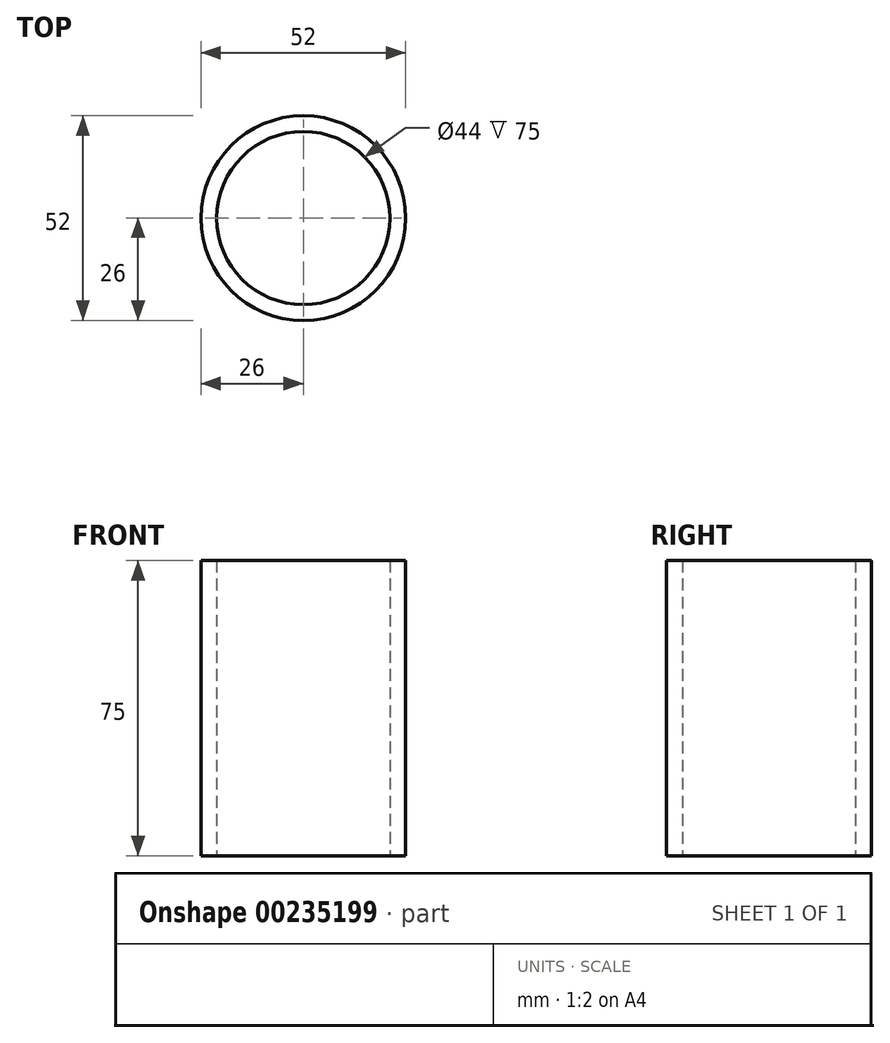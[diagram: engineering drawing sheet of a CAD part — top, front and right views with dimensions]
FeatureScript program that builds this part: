
annotation { "Feature Type Name" : "Feature", "Feature Type Description" : "" }
export const myFeature = defineFeature(function(context is Context, id is Id, definition is map)
    precondition{}
    {
        {
            var Q0;
            Q0=qCreatedBy(makeId("Top.planeOp"),FACE);
            var sketch = newSketch(context, id + "F0", { "sketchPlane" : qUnion([Q0])});
            skCircle(sketch, "E0", {"center": v(0, 0) * mm, "radius": 26 * mm});
            skSolve(sketch);
        }
        {
            var Q0;
            Q0=makeQuery(id+"F0.imprint","IMPRINT",FACE,{"disambiguationData":[TD([[makeQuery(id+"F0.imprint","IMPRINT",EDGE,{"derivedFrom":sQuery(id+"F0.wireOp",EDGE,"E0")}),1.0]])]});
            extrude(context, id + "F1", {"entities" : qUnion([Q0]), "depth" : 75 * mm});
        }
        {
            var Q0;
            Q0=makeQuery(id+"F1.opExtrude","CAP_FACE",FACE,{"disambiguationData":[OSD([sQuery(id+"F0.wireOp",EDGE,"E0")])],"isStart":true});
            var Q1;
            Q1=makeQuery(id+"F1.opExtrude","CAP_FACE",FACE,{"disambiguationData":[OSD([sQuery(id+"F0.wireOp",EDGE,"E0")])],"isStart":false});
            shell(context, id + "F2", {"entities" : qUnion([Q0, Q1]), "thickness" : 4 * mm});
        }
    });
